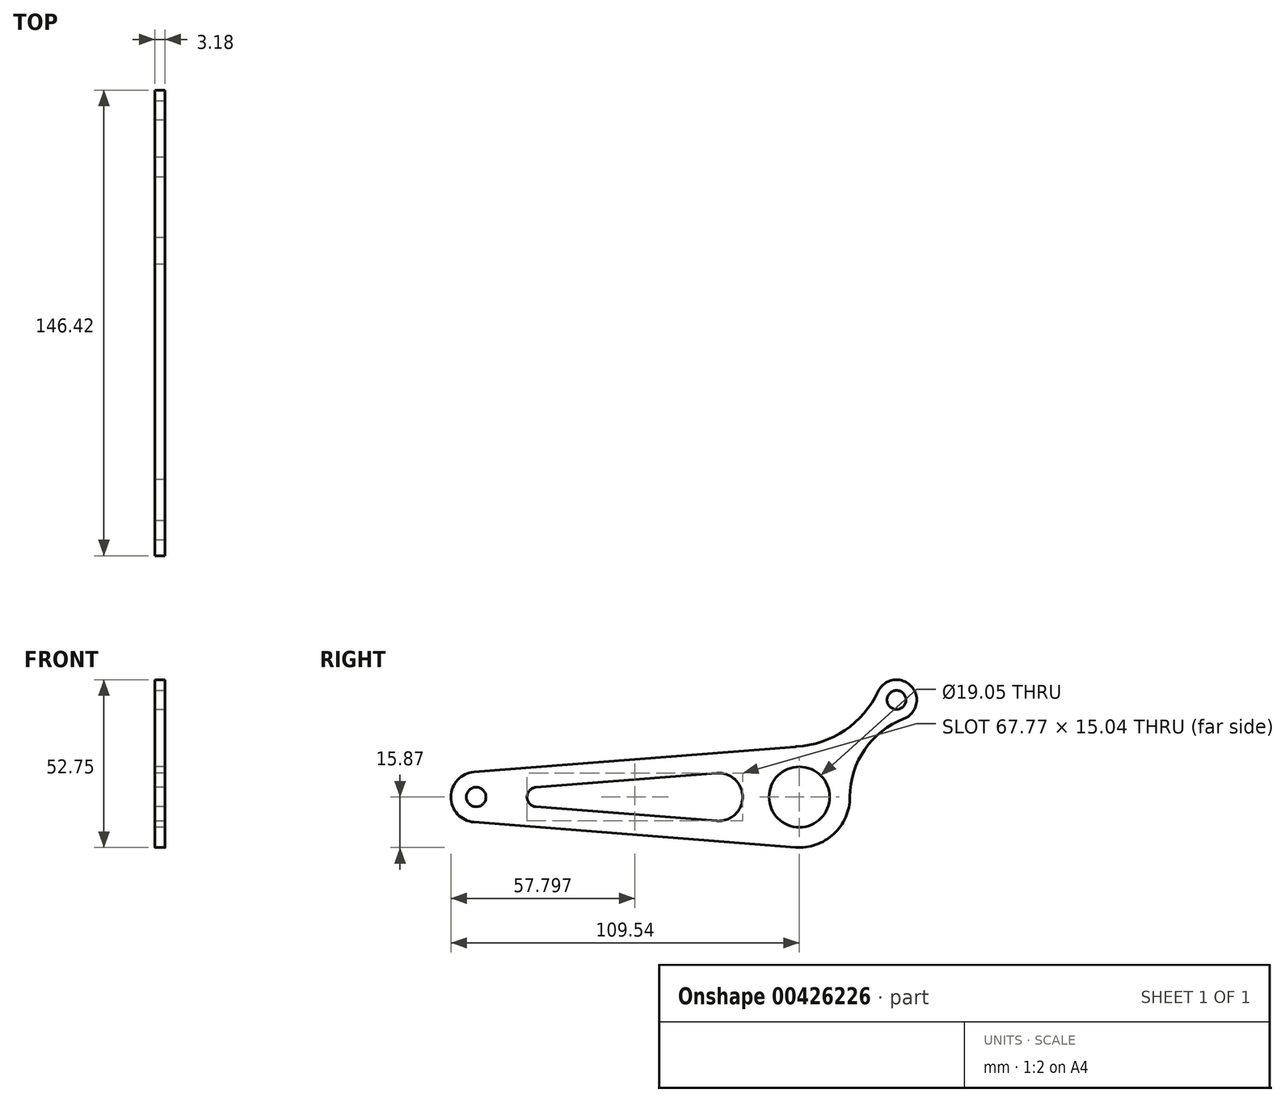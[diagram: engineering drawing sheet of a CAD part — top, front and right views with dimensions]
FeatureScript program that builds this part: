
annotation { "Feature Type Name" : "Feature", "Feature Type Description" : "" }
export const myFeature = defineFeature(function(context is Context, id is Id, definition is map)
    precondition{}
    {
        {
            var Q0;
            Q0=qCreatedBy(makeId("Right.planeOp"),FACE);
            var sketch = newSketch(context, id + "F0", { "sketchPlane" : qUnion([Q0])});
            skCircle(sketch, "E0", {"center": v(0, 0) * mm, "radius": 9.53 * mm});
            skArc(sketch, "E1", {"start": v(-1.24, -15.83) * mm, "mid": v(9.86, -12.45) * mm, "end": v(15.69, -2.42) * mm});
            skArc(sketch, "E2", {"start": v(-102.22, 7.91) * mm, "mid": v(-109.54, 0) * mm, "end": v(-102.22, -7.91) * mm});
            skCircle(sketch, "E3", {"center": v(-101.6, 0) * mm, "radius": 3.09 * mm});
            skLineSegment(sketch, "E4", {"start": v(-1.24, -15.83) * mm, "end": v(-102.22, -7.91) * mm});
            skLineSegment(sketch, "E5", {"start": v(-1.24, 15.83) * mm, "end": v(-102.22, 7.91) * mm});
            skArc(sketch, "E6", {"start": v(-25.99, -7.52) * mm, "mid": v(-17.86, 0) * mm, "end": v(-25.99, 7.52) * mm});
            skLineSegment(sketch, "E7.trimOffspring", {"start": v(-25.99, -7.52) * mm, "end": v(-82.8, -3.07) * mm});
            skLineSegment(sketch, "E8.trimOffspring", {"start": v(-25.99, 7.52) * mm, "end": v(-82.8, 3.07) * mm});
            skArc(sketch, "E9.filletArc", {"start": v(-82.8, 3.07) * mm, "mid": v(-85.63, 0) * mm, "end": v(-82.8, -3.07) * mm});
            skArc(sketch, "E10", {"start": v(-1.24, -15.83) * mm, "mid": v(10.66, -11.77) * mm, "end": v(15.87, -0.33) * mm});
            skArc(sketch, "E11.trimOffspring", {"start": v(15.87, -0.48) * mm, "mid": v(10.95, 11.5) * mm, "end": v(-1.24, 15.83) * mm});
            skLineSegment(sketch, "E12", {"start": v(0, 0) * mm, "end": v(0, 50.2) * mm, "construction": true});
            skLineSegment(sketch, "E13", {"start": v(0, 0) * mm, "end": v(111.24, 0) * mm, "construction": true});
            skLineSegment(sketch, "E14", {"start": v(0, 0) * mm, "end": v(-53.6, 0) * mm, "construction": true});
            skLineSegment(sketch, "E15", {"start": v(-53.6, 0) * mm, "end": v(-101.6, 22.8) * mm, "construction": true});
            skSolve(sketch);
        }
        {
            var Q0;
            Q0 = qSketchRegion(id + "F0", true);
            extrude(context, id + "F1", {"entities" : qUnion([Q0]), "offsetDistance" : 25.4 * mm, "depth" : 3.17 * mm});
        }
        {
            var Q0;
            Q0=makeQuery(id+"F1.opExtrude","CAP_FACE",FACE,{"disambiguationData":[OSD([sQuery(id+"F0.wireOp",EDGE,"E0"),sQuery(id+"F0.wireOp",EDGE,"E2"),sQuery(id+"F0.wireOp",EDGE,"E3"),sQuery(id+"F0.wireOp",EDGE,"E4"),sQuery(id+"F0.wireOp",EDGE,"E5"),sQuery(id+"F0.wireOp",EDGE,"E6"),sQuery(id+"F0.wireOp",EDGE,"E7.trimOffspring"),sQuery(id+"F0.wireOp",EDGE,"E8.trimOffspring"),sQuery(id+"F0.wireOp",EDGE,"E9.filletArc"),sQuery(id+"F0.wireOp",EDGE,"E10"),sQuery(id+"F0.wireOp",EDGE,"E11.trimOffspring")])],"isStart":false});
            var sketch = newSketch(context, id + "F2", { "sketchPlane" : qUnion([Q0])});
            skLineSegment(sketch, "E16", {"start": v(0, 0) * mm, "end": v(0, 40.26) * mm, "construction": true});
            skArc(sketch, "E17.MirrorC", {"start": v(24.78, 33.23) * mm, "mid": v(35.18, 34.86) * mm, "end": v(32.8, 24.6) * mm});
            skCircle(sketch, "E18.MirrorC", {"center": v(30.53, 30.53) * mm, "radius": 2.98 * mm});
            skArc(sketch, "E19.MirrorCS", {"start": v(24.78, 33.23) * mm, "mid": v(14.34, 21) * mm, "end": v(-0.9, 15.85) * mm});
            skArc(sketch, "E20.MirrorCS", {"start": v(-0.9, 15.85) * mm, "mid": v(10.9, 11.54) * mm, "end": v(15.87, 0) * mm});
            skArc(sketch, "E21.MirrorCS", {"start": v(15.87, 0) * mm, "mid": v(20.52, 14.93) * mm, "end": v(32.8, 24.6) * mm});
            skLineSegment(sketch, "E22.MirrorCS", {"start": v(0, 0) * mm, "end": v(30.53, 30.53) * mm, "construction": true});
            skLineSegment(sketch, "E23.MirrorCS", {"start": v(0, 0) * mm, "end": v(41.94, 0) * mm, "construction": true});
            skPoint(sketch, "E24.orphan", {"position": v(0.9, 15.85) * mm});
            skSolve(sketch);
        }
        {
            var Q0;
            Q0 = qSketchRegion(id + "F2", true);
            extrude(context, id + "F3", {"entities" : qUnion([Q0]), "operationType" : NewBodyOperationType.ADD, "oppositeDirection" : true, "depth" : 3.17 * mm});
        }
    });
